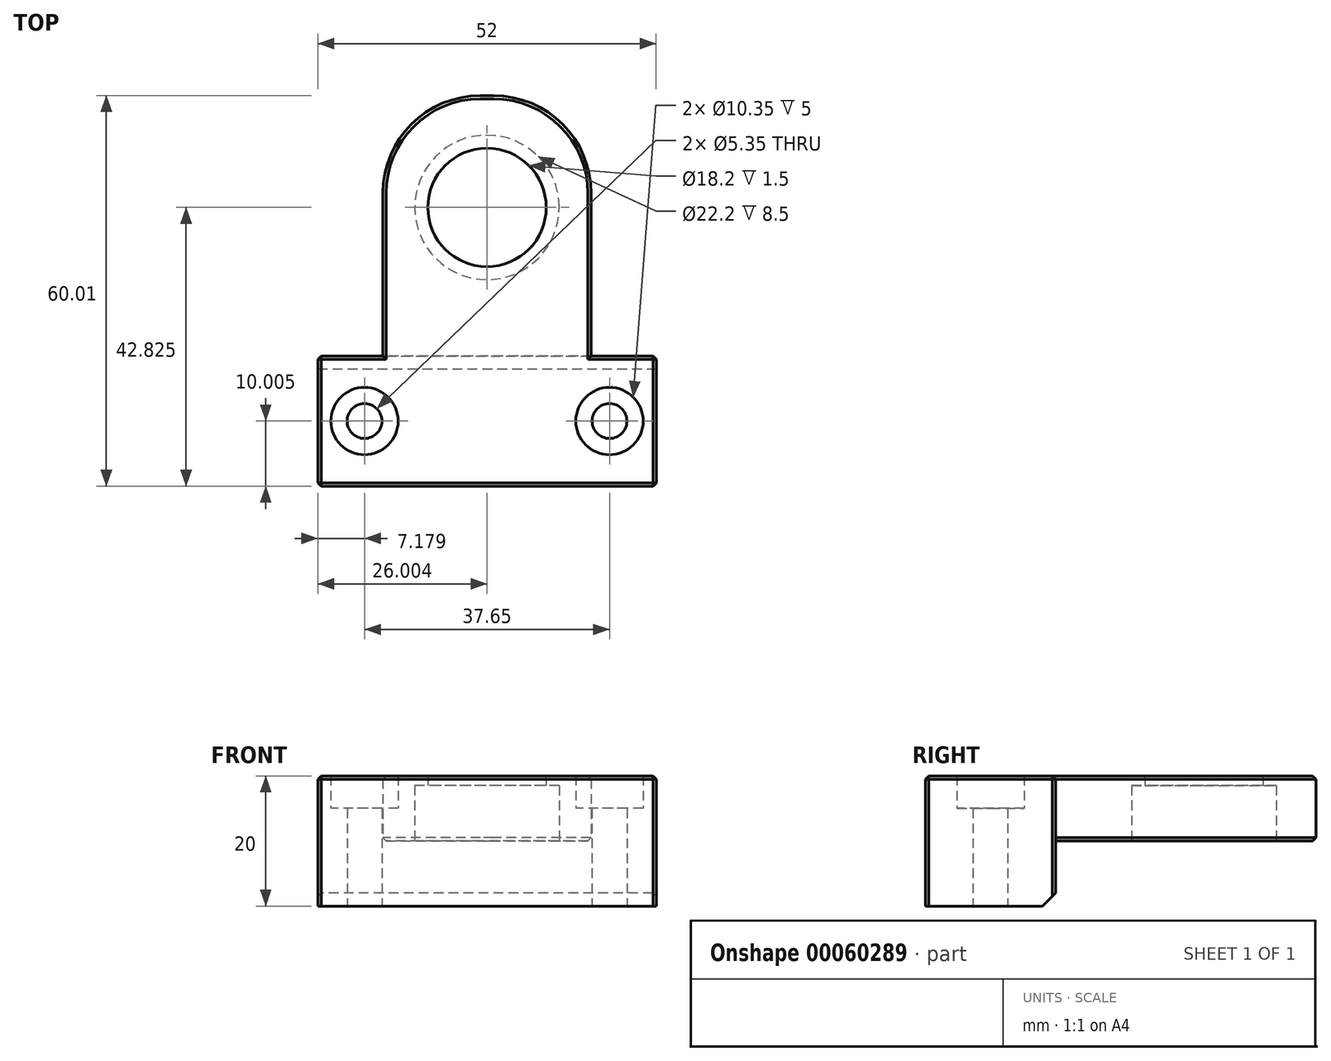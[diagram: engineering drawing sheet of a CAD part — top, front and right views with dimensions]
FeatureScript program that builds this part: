
annotation { "Feature Type Name" : "Feature", "Feature Type Description" : "" }
export const myFeature = defineFeature(function(context is Context, id is Id, definition is map)
    precondition{}
    {
        {
            var Q0;
            Q0=qCreatedBy(makeId("Top.planeOp"),FACE);
            var sketch = newSketch(context, id + "F0", { "sketchPlane" : qUnion([Q0])});
            skLineSegment(sketch, "E0.bottom", {"start": v(-17.08, 30.82) * mm, "end": v(14.92, 30.82) * mm});
            skLineSegment(sketch, "E0.left", {"start": v(-17.08, 30.82) * mm, "end": v(-17.08, -9.18) * mm});
            skLineSegment(sketch, "E1", {"start": v(-17.08, -29.18) * mm, "end": v(14.92, -29.17) * mm});
            skCircle(sketch, "E2", {"center": v(-19.9, -19.18) * mm, "radius": 2.67 * mm});
            skCircle(sketch, "E3", {"center": v(17.75, -19.17) * mm, "radius": 2.67 * mm});
            skLineSegment(sketch, "E4", {"start": v(14.92, -9.17) * mm, "end": v(24.92, -9.17) * mm});
            skLineSegment(sketch, "E5", {"start": v(24.92, -9.17) * mm, "end": v(24.92, -29.17) * mm});
            skLineSegment(sketch, "E6", {"start": v(24.92, -29.17) * mm, "end": v(14.92, -29.17) * mm});
            skCircle(sketch, "E7", {"center": v(-19.9, -19.18) * mm, "radius": 5.17 * mm});
            skCircle(sketch, "E8", {"center": v(17.75, -19.17) * mm, "radius": 5.17 * mm});
            skLineSegment(sketch, "E9", {"start": v(-17.08, -9.18) * mm, "end": v(-27.08, -9.18) * mm});
            skLineSegment(sketch, "E10", {"start": v(-27.08, -9.18) * mm, "end": v(-27.08, -29.18) * mm});
            skLineSegment(sketch, "E11", {"start": v(-27.08, -29.18) * mm, "end": v(-17.08, -29.18) * mm});
            skLineSegment(sketch, "E12", {"start": v(-17.08, -9.18) * mm, "end": v(14.92, -9.17) * mm});
            skLineSegment(sketch, "E13", {"start": v(14.92, 30.82) * mm, "end": v(14.92, -9.17) * mm});
            skCircle(sketch, "E14", {"center": v(-1.08, 13.64) * mm, "radius": 9.1 * mm});
            skCircle(sketch, "E15", {"center": v(-1.08, 13.64) * mm, "radius": 11.1 * mm});
            skSolve(sketch);
        }
        {
            var Q0;
            Q0=qSketchRegion(id+"F0",true);
            extrude(context, id + "F1", {"entities" : qUnion([Q0]), "depth" : 10 * mm});
        }
        {
            var Q0;
            Q0=makeQuery(id+"F0.imprint","IMPRINT",FACE,{"disambiguationData":[TD([[makeQuery(id+"F0.imprint","IMPRINT",EDGE,{"derivedFrom":sQuery(id+"F0.wireOp",EDGE,"E2")}),-1.0]])]});
            extrude(context, id + "F2", {"entities" : qUnion([Q0]), "operationType" : NewBodyOperationType.ADD, "depth" : 5 * mm});
        }
        {
            var Q0;
            Q0=makeQuery(id+"F0.imprint","IMPRINT",FACE,{"disambiguationData":[TD([[makeQuery(id+"F0.imprint","IMPRINT",EDGE,{"derivedFrom":sQuery(id+"F0.wireOp",EDGE,"E3")}),-1.0]])]});
            extrude(context, id + "F3", {"entities" : qUnion([Q0]), "operationType" : NewBodyOperationType.ADD, "depth" : 5 * mm});
        }
        {
            var Q0;
            Q0=makeQuery(id+"F1.opExtrude","CAP_EDGE",EDGE,{"disambiguationData":[OSD([sQuery(id+"F0.wireOp",EDGE,"E10")])],"isStart":false});
            var Q1;
            Q1=makeQuery(id+"F1.opExtrude","CAP_EDGE",EDGE,{"disambiguationData":[OSD([sQuery(id+"F0.wireOp",EDGE,"E9")])],"isStart":false});
            var Q2;
            Q2=makeQuery(id+"F1.opExtrude","CAP_EDGE",EDGE,{"disambiguationData":[OSD([sQuery(id+"F0.wireOp",EDGE,"E4")])],"isStart":false});
            var Q3;
            Q3=makeQuery(id+"F1.opExtrude","CAP_EDGE",EDGE,{"disambiguationData":[OSD([sQuery(id+"F0.wireOp",EDGE,"E5")])],"isStart":false});
            var Q4;
            Q4=makeQuery(id+"F1.opExtrude","SWEPT_EDGE",EDGE,{"disambiguationData":[OSD([sQuery(id+"F0.wireOp",EDGE,"E4"),sQuery(id+"F0.wireOp",EDGE,"E5")])]});
            var Q5;
            Q5=makeQuery(id+"F1.opExtrude","SWEPT_EDGE",EDGE,{"disambiguationData":[OSD([sQuery(id+"F0.wireOp",EDGE,"E4"),sQuery(id+"F0.wireOp",EDGE,"E5")])]});
            var Q6;
            Q6=makeQuery(id+"F1.opExtrude","SWEPT_EDGE",EDGE,{"disambiguationData":[OSD([sQuery(id+"F0.wireOp",EDGE,"E9"),sQuery(id+"F0.wireOp",EDGE,"E10")])]});
            var Q7;
            Q7=makeQuery(id+"F1.opExtrude","SWEPT_EDGE",EDGE,{"disambiguationData":[OSD([sQuery(id+"F0.wireOp",EDGE,"E10"),sQuery(id+"F0.wireOp",EDGE,"E11")])]});
            var Q8;
            Q8=makeQuery(id+"F1.opExtrude","SWEPT_EDGE",EDGE,{"disambiguationData":[OSD([sQuery(id+"F0.wireOp",EDGE,"E5"),sQuery(id+"F0.wireOp",EDGE,"E6")])]});
            var Q9;
            Q9=makeQuery(id+"F1.opExtrude","CAP_EDGE",EDGE,{"disambiguationData":[OSD([sQuery(id+"F0.wireOp",EDGE,"E1"),sQuery(id+"F0.wireOp",EDGE,"E6"),sQuery(id+"F0.wireOp",EDGE,"E11")])],"isStart":false});
            var Q10;
            Q10=makeQuery(id+"F1.opExtrude","CAP_EDGE",EDGE,{"disambiguationData":[OSD([sQuery(id+"F0.wireOp",EDGE,"E0.left")])],"isStart":false});
            var Q11;
            Q11=makeQuery(id+"F1.opExtrude","CAP_EDGE",EDGE,{"disambiguationData":[OSD([sQuery(id+"F0.wireOp",EDGE,"E13")])],"isStart":false});
            chamfer(context, id + "F4", {"entities" : qUnion([Q0, Q1, Q2, Q3, Q4, Q5, Q6, Q7, Q8, Q9, Q10, Q11]), "width" : 0.5 * mm, "tangentPropagation" : true});
        }
        {
            var Q0;
            Q0=makeQuery(id+"F0.imprint","IMPRINT",FACE,{"disambiguationData":[TD([[makeQuery(id+"F0.imprint","IMPRINT",EDGE,{"derivedFrom":sQuery(id+"F0.wireOp",EDGE,"E1")}),1.0]])]});
            extrude(context, id + "F5", {"entities" : qUnion([Q0]), "operationType" : NewBodyOperationType.ADD, "oppositeDirection" : true, "depth" : 10 * mm});
        }
        {
            var Q0;
            Q0=makeQuery(id+"F0.imprint","IMPRINT",FACE,{"disambiguationData":[TD([[makeQuery(id+"F0.imprint","IMPRINT",EDGE,{"derivedFrom":sQuery(id+"F0.wireOp",EDGE,"E3")}),-1.0]])]});
            var Q1;
            Q1=makeQuery(id+"F0.imprint","IMPRINT",FACE,{"disambiguationData":[TD([[makeQuery(id+"F0.imprint","IMPRINT",EDGE,{"derivedFrom":sQuery(id+"F0.wireOp",EDGE,"E2")}),-1.0]])]});
            extrude(context, id + "F6", {"entities" : qUnion([Q0, Q1]), "operationType" : NewBodyOperationType.ADD, "oppositeDirection" : true, "depth" : 10 * mm});
        }
        {
            var Q0;
            Q0=makeQuery(id+"F5.opExtrude","SWEPT_EDGE",EDGE,{"disambiguationData":[OSD([sQuery(id+"F0.wireOp",EDGE,"E4"),sQuery(id+"F0.wireOp",EDGE,"E5")])]});
            var Q1;
            Q1=makeQuery(id+"F5.opExtrude","SWEPT_EDGE",EDGE,{"disambiguationData":[OSD([sQuery(id+"F0.wireOp",EDGE,"E9"),sQuery(id+"F0.wireOp",EDGE,"E10")])]});
            var Q2;
            Q2=makeQuery(id+"F5.opExtrude","SWEPT_EDGE",EDGE,{"disambiguationData":[OSD([sQuery(id+"F0.wireOp",EDGE,"E5"),sQuery(id+"F0.wireOp",EDGE,"E6")])]});
            var Q3;
            Q3=makeQuery(id+"F5.opExtrude","SWEPT_EDGE",EDGE,{"disambiguationData":[OSD([sQuery(id+"F0.wireOp",EDGE,"E10"),sQuery(id+"F0.wireOp",EDGE,"E11")])]});
            chamfer(context, id + "F7", {"entities" : qUnion([Q0, Q1, Q2, Q3]), "width" : 0.5 * mm, "tangentPropagation" : true});
        }
        {
            var Q0;
            Q0=makeQuery(id+"F5.opExtrude","CAP_EDGE",EDGE,{"disambiguationData":[OSD([sQuery(id+"F0.wireOp",EDGE,"E4"),sQuery(id+"F0.wireOp",EDGE,"E9"),sQuery(id+"F0.wireOp",EDGE,"E12")])],"isStart":false});
            chamfer(context, id + "F8", {"entities" : qUnion([Q0]), "width" : 2 * mm, "tangentPropagation" : true});
        }
        {
            var Q0;
            Q0=makeQuery(id+"F0.imprint","IMPRINT",FACE,{"disambiguationData":[TD([[makeQuery(id+"F0.imprint","IMPRINT",EDGE,{"derivedFrom":sQuery(id+"F0.wireOp",EDGE,"E14")}),-1.0]])]});
            extrude(context, id + "F9", {"entities" : qUnion([Q0]), "operationType" : NewBodyOperationType.ADD, "depth" : 10 * mm});
        }
        {
            var Q0;
            Q0=makeQuery(id+"F0.imprint","IMPRINT",FACE,{"disambiguationData":[TD([[makeQuery(id+"F0.imprint","IMPRINT",EDGE,{"derivedFrom":sQuery(id+"F0.wireOp",EDGE,"E14")}),-1.0]])]});
            extrude(context, id + "F10", {"entities" : qUnion([Q0]), "operationType" : NewBodyOperationType.REMOVE, "depth" : 8.5 * mm});
        }
        {
            var Q0;
            Q0=makeQuery(id+"F1.opExtrude","SWEPT_EDGE",EDGE,{"disambiguationData":[OSD([sQuery(id+"F0.wireOp",EDGE,"E0.bottom"),sQuery(id+"F0.wireOp",EDGE,"E13")])]});
            var Q1;
            Q1=makeQuery(id+"F1.opExtrude","SWEPT_EDGE",EDGE,{"disambiguationData":[OSD([sQuery(id+"F0.wireOp",EDGE,"E0.bottom"),sQuery(id+"F0.wireOp",EDGE,"E0.left")])]});
            fillet(context, id + "F11", {"entities" : qUnion([Q0, Q1]), "radius" : 15 * mm, "tangentPropagation" : true, "allowEdgeOverflow" : false});
        }
        {
            var Q0;
            {var subQ0=sQuery(id+"F0.wireOp",EDGE,"E15");var subQ1=sQuery(id+"F0.wireOp",EDGE,"E13");var subQ2=sQuery(id+"F0.wireOp",EDGE,"E4");var subQ3=sQuery(id+"F0.wireOp",EDGE,"E9");var subQ4=sQuery(id+"F0.wireOp",EDGE,"E0.left");var subQ6=sQuery(id+"F0.wireOp",EDGE,"E0.bottom");var subQ7=sQuery(id+"F0.wireOp",EDGE,"E8");var subQ8=sQuery(id+"F0.wireOp",EDGE,"E7");Q0=makeQuery(id+"F11.opFillet","BLEND_EDGE",EDGE,{"blendedFrom":[makeQuery(id+"F1.opExtrude","SWEPT_EDGE",EDGE,{"disambiguationData":[OSD([subQ6,subQ1])]}),makeQuery(id+"F9.boolean.opBoolean","MERGE",FACE,{"derivedFrom":[makeQuery(id+"F5.boolean.opBoolean","SPLIT",FACE,{"disambiguationData":[TD([makeQuery(id+"F1.opExtrude","SWEPT_FACE",FACE,{"disambiguationData":[OSD([subQ4])]})])],"derivedFrom":makeQuery(id+"F3.boolean.opBoolean","MERGE",FACE,{"derivedFrom":[makeQuery(id+"F2.boolean.opBoolean","MERGE",FACE,{"derivedFrom":[makeQuery(id+"F1.opExtrude","CAP_FACE",FACE,{"disambiguationData":[OSD([subQ6,subQ4,sQuery(id+"F0.wireOp",EDGE,"E1"),subQ2,sQuery(id+"F0.wireOp",EDGE,"E5"),sQuery(id+"F0.wireOp",EDGE,"E6"),subQ8,subQ7,subQ3,sQuery(id+"F0.wireOp",EDGE,"E10"),sQuery(id+"F0.wireOp",EDGE,"E11"),subQ1,subQ0])],"isStart":true}),makeQuery(id+"F2.opExtrude","CAP_FACE",FACE,{"disambiguationData":[OSD([sQuery(id+"F0.wireOp",EDGE,"E2"),subQ8])],"isStart":true})]}),makeQuery(id+"F3.opExtrude","CAP_FACE",FACE,{"disambiguationData":[OSD([sQuery(id+"F0.wireOp",EDGE,"E3"),subQ7])],"isStart":true})]})}),makeQuery(id+"F9.opExtrude","CAP_FACE",FACE,{"disambiguationData":[OSD([sQuery(id+"F0.wireOp",EDGE,"E14"),subQ0])],"isStart":true})]})],"blendedInto":[makeQuery(id+"F9.boolean.opBoolean","MERGE",FACE,{"derivedFrom":[makeQuery(id+"F5.boolean.opBoolean","SPLIT",FACE,{"disambiguationData":[TD([makeQuery(id+"F1.opExtrude","SWEPT_FACE",FACE,{"disambiguationData":[OSD([subQ4])]})])],"derivedFrom":makeQuery(id+"F3.boolean.opBoolean","MERGE",FACE,{"derivedFrom":[makeQuery(id+"F2.boolean.opBoolean","MERGE",FACE,{"derivedFrom":[makeQuery(id+"F1.opExtrude","CAP_FACE",FACE,{"disambiguationData":[OSD([subQ6,subQ4,sQuery(id+"F0.wireOp",EDGE,"E1"),subQ2,sQuery(id+"F0.wireOp",EDGE,"E5"),sQuery(id+"F0.wireOp",EDGE,"E6"),subQ8,subQ7,subQ3,sQuery(id+"F0.wireOp",EDGE,"E10"),sQuery(id+"F0.wireOp",EDGE,"E11"),subQ1,subQ0])],"isStart":true}),makeQuery(id+"F2.opExtrude","CAP_FACE",FACE,{"disambiguationData":[OSD([sQuery(id+"F0.wireOp",EDGE,"E2"),subQ8])],"isStart":true})]}),makeQuery(id+"F3.opExtrude","CAP_FACE",FACE,{"disambiguationData":[OSD([sQuery(id+"F0.wireOp",EDGE,"E3"),subQ7])],"isStart":true})]})}),makeQuery(id+"F9.opExtrude","CAP_FACE",FACE,{"disambiguationData":[OSD([sQuery(id+"F0.wireOp",EDGE,"E14"),subQ0])],"isStart":true})]})]});}
            var Q1;
            {var subQ0=sQuery(id+"F0.wireOp",EDGE,"E15");var subQ1=sQuery(id+"F0.wireOp",EDGE,"E0.left");var subQ2=sQuery(id+"F0.wireOp",EDGE,"E0.bottom");Q1=makeQuery(id+"F11.opFillet","BLEND_EDGE",EDGE,{"blendedFrom":[makeQuery(id+"F1.opExtrude","SWEPT_EDGE",EDGE,{"disambiguationData":[OSD([subQ2,subQ1])]}),makeQuery(id+"F9.boolean.opBoolean","MERGE",FACE,{"derivedFrom":[makeQuery(id+"F1.opExtrude","CAP_FACE",FACE,{"disambiguationData":[OSD([subQ2,subQ1,sQuery(id+"F0.wireOp",EDGE,"E1"),sQuery(id+"F0.wireOp",EDGE,"E4"),sQuery(id+"F0.wireOp",EDGE,"E5"),sQuery(id+"F0.wireOp",EDGE,"E6"),sQuery(id+"F0.wireOp",EDGE,"E7"),sQuery(id+"F0.wireOp",EDGE,"E8"),sQuery(id+"F0.wireOp",EDGE,"E9"),sQuery(id+"F0.wireOp",EDGE,"E10"),sQuery(id+"F0.wireOp",EDGE,"E11"),sQuery(id+"F0.wireOp",EDGE,"E13"),subQ0])],"isStart":false}),makeQuery(id+"F9.opExtrude","CAP_FACE",FACE,{"disambiguationData":[OSD([sQuery(id+"F0.wireOp",EDGE,"E14"),subQ0])],"isStart":false})]})],"blendedInto":[makeQuery(id+"F9.boolean.opBoolean","MERGE",FACE,{"derivedFrom":[makeQuery(id+"F1.opExtrude","CAP_FACE",FACE,{"disambiguationData":[OSD([subQ2,subQ1,sQuery(id+"F0.wireOp",EDGE,"E1"),sQuery(id+"F0.wireOp",EDGE,"E4"),sQuery(id+"F0.wireOp",EDGE,"E5"),sQuery(id+"F0.wireOp",EDGE,"E6"),sQuery(id+"F0.wireOp",EDGE,"E7"),sQuery(id+"F0.wireOp",EDGE,"E8"),sQuery(id+"F0.wireOp",EDGE,"E9"),sQuery(id+"F0.wireOp",EDGE,"E10"),sQuery(id+"F0.wireOp",EDGE,"E11"),sQuery(id+"F0.wireOp",EDGE,"E13"),subQ0])],"isStart":false}),makeQuery(id+"F9.opExtrude","CAP_FACE",FACE,{"disambiguationData":[OSD([sQuery(id+"F0.wireOp",EDGE,"E14"),subQ0])],"isStart":false})]})]});}
            var Q2;
            {var subQ0=sQuery(id+"F0.wireOp",EDGE,"E15");var subQ1=sQuery(id+"F0.wireOp",EDGE,"E13");var subQ2=sQuery(id+"F0.wireOp",EDGE,"E0.bottom");Q2=makeQuery(id+"F11.opFillet","BLEND_EDGE",EDGE,{"blendedFrom":[makeQuery(id+"F1.opExtrude","SWEPT_EDGE",EDGE,{"disambiguationData":[OSD([subQ2,subQ1])]}),makeQuery(id+"F9.boolean.opBoolean","MERGE",FACE,{"derivedFrom":[makeQuery(id+"F1.opExtrude","CAP_FACE",FACE,{"disambiguationData":[OSD([subQ2,sQuery(id+"F0.wireOp",EDGE,"E0.left"),sQuery(id+"F0.wireOp",EDGE,"E1"),sQuery(id+"F0.wireOp",EDGE,"E4"),sQuery(id+"F0.wireOp",EDGE,"E5"),sQuery(id+"F0.wireOp",EDGE,"E6"),sQuery(id+"F0.wireOp",EDGE,"E7"),sQuery(id+"F0.wireOp",EDGE,"E8"),sQuery(id+"F0.wireOp",EDGE,"E9"),sQuery(id+"F0.wireOp",EDGE,"E10"),sQuery(id+"F0.wireOp",EDGE,"E11"),subQ1,subQ0])],"isStart":false}),makeQuery(id+"F9.opExtrude","CAP_FACE",FACE,{"disambiguationData":[OSD([sQuery(id+"F0.wireOp",EDGE,"E14"),subQ0])],"isStart":false})]})],"blendedInto":[makeQuery(id+"F9.boolean.opBoolean","MERGE",FACE,{"derivedFrom":[makeQuery(id+"F1.opExtrude","CAP_FACE",FACE,{"disambiguationData":[OSD([subQ2,sQuery(id+"F0.wireOp",EDGE,"E0.left"),sQuery(id+"F0.wireOp",EDGE,"E1"),sQuery(id+"F0.wireOp",EDGE,"E4"),sQuery(id+"F0.wireOp",EDGE,"E5"),sQuery(id+"F0.wireOp",EDGE,"E6"),sQuery(id+"F0.wireOp",EDGE,"E7"),sQuery(id+"F0.wireOp",EDGE,"E8"),sQuery(id+"F0.wireOp",EDGE,"E9"),sQuery(id+"F0.wireOp",EDGE,"E10"),sQuery(id+"F0.wireOp",EDGE,"E11"),subQ1,subQ0])],"isStart":false}),makeQuery(id+"F9.opExtrude","CAP_FACE",FACE,{"disambiguationData":[OSD([sQuery(id+"F0.wireOp",EDGE,"E14"),subQ0])],"isStart":false})]})]});}
            var Q3;
            Q3=makeQuery(id+"F1.opExtrude","CAP_EDGE",EDGE,{"disambiguationData":[OSD([sQuery(id+"F0.wireOp",EDGE,"E0.bottom")])],"isStart":false});
            var Q4;
            Q4=makeQuery(id+"F1.opExtrude","CAP_EDGE",EDGE,{"disambiguationData":[OSD([sQuery(id+"F0.wireOp",EDGE,"E0.bottom")])],"isStart":true});
            var Q5;
            {var subQ0=sQuery(id+"F0.wireOp",EDGE,"E15");var subQ1=sQuery(id+"F0.wireOp",EDGE,"E4");var subQ2=sQuery(id+"F0.wireOp",EDGE,"E9");var subQ3=sQuery(id+"F0.wireOp",EDGE,"E0.left");var subQ5=sQuery(id+"F0.wireOp",EDGE,"E0.bottom");var subQ6=sQuery(id+"F0.wireOp",EDGE,"E13");var subQ7=sQuery(id+"F0.wireOp",EDGE,"E8");var subQ8=sQuery(id+"F0.wireOp",EDGE,"E7");Q5=makeQuery(id+"F11.opFillet","BLEND_EDGE",EDGE,{"blendedFrom":[makeQuery(id+"F1.opExtrude","SWEPT_EDGE",EDGE,{"disambiguationData":[OSD([subQ5,subQ3])]}),makeQuery(id+"F9.boolean.opBoolean","MERGE",FACE,{"derivedFrom":[makeQuery(id+"F5.boolean.opBoolean","SPLIT",FACE,{"disambiguationData":[TD([makeQuery(id+"F1.opExtrude","SWEPT_FACE",FACE,{"disambiguationData":[OSD([subQ5])]})])],"derivedFrom":makeQuery(id+"F3.boolean.opBoolean","MERGE",FACE,{"derivedFrom":[makeQuery(id+"F2.boolean.opBoolean","MERGE",FACE,{"derivedFrom":[makeQuery(id+"F1.opExtrude","CAP_FACE",FACE,{"disambiguationData":[OSD([subQ5,subQ3,sQuery(id+"F0.wireOp",EDGE,"E1"),subQ1,sQuery(id+"F0.wireOp",EDGE,"E5"),sQuery(id+"F0.wireOp",EDGE,"E6"),subQ8,subQ7,subQ2,sQuery(id+"F0.wireOp",EDGE,"E10"),sQuery(id+"F0.wireOp",EDGE,"E11"),subQ6,subQ0])],"isStart":true}),makeQuery(id+"F2.opExtrude","CAP_FACE",FACE,{"disambiguationData":[OSD([sQuery(id+"F0.wireOp",EDGE,"E2"),subQ8])],"isStart":true})]}),makeQuery(id+"F3.opExtrude","CAP_FACE",FACE,{"disambiguationData":[OSD([sQuery(id+"F0.wireOp",EDGE,"E3"),subQ7])],"isStart":true})]})}),makeQuery(id+"F9.opExtrude","CAP_FACE",FACE,{"disambiguationData":[OSD([sQuery(id+"F0.wireOp",EDGE,"E14"),subQ0])],"isStart":true})]})],"blendedInto":[makeQuery(id+"F9.boolean.opBoolean","MERGE",FACE,{"derivedFrom":[makeQuery(id+"F5.boolean.opBoolean","SPLIT",FACE,{"disambiguationData":[TD([makeQuery(id+"F1.opExtrude","SWEPT_FACE",FACE,{"disambiguationData":[OSD([subQ5])]})])],"derivedFrom":makeQuery(id+"F3.boolean.opBoolean","MERGE",FACE,{"derivedFrom":[makeQuery(id+"F2.boolean.opBoolean","MERGE",FACE,{"derivedFrom":[makeQuery(id+"F1.opExtrude","CAP_FACE",FACE,{"disambiguationData":[OSD([subQ5,subQ3,sQuery(id+"F0.wireOp",EDGE,"E1"),subQ1,sQuery(id+"F0.wireOp",EDGE,"E5"),sQuery(id+"F0.wireOp",EDGE,"E6"),subQ8,subQ7,subQ2,sQuery(id+"F0.wireOp",EDGE,"E10"),sQuery(id+"F0.wireOp",EDGE,"E11"),subQ6,subQ0])],"isStart":true}),makeQuery(id+"F2.opExtrude","CAP_FACE",FACE,{"disambiguationData":[OSD([sQuery(id+"F0.wireOp",EDGE,"E2"),subQ8])],"isStart":true})]}),makeQuery(id+"F3.opExtrude","CAP_FACE",FACE,{"disambiguationData":[OSD([sQuery(id+"F0.wireOp",EDGE,"E3"),subQ7])],"isStart":true})]})}),makeQuery(id+"F9.opExtrude","CAP_FACE",FACE,{"disambiguationData":[OSD([sQuery(id+"F0.wireOp",EDGE,"E14"),subQ0])],"isStart":true})]})]});}
            chamfer(context, id + "F12", {"entities" : qUnion([Q0, Q1, Q2, Q3, Q4, Q5]), "width" : 0.5 * mm, "tangentPropagation" : true});
        }
    });
